# Revit family: 931-10-001 DN50-80
name_source: partatom
category: Pipe Accessories
units: mm (PartAtom-declared; Revit-internal decimal feet)

## family parameters
Always vertical = Yes
Cut with Voids When Loaded = No
Part Type = Valve - Breaks Into
Round Connector Dimension = Use Diameter
Shared = No
Work Plane-Based = No

## types (3) — shared parameters
1 = 1 mm  [stored 0.00328084 ft]
2 = 3 mm  [stored 0.00984252 ft]
Actuator_Flange_R = 45 mm  [stored 0.147638 ft]
Body_Thickness = 6 mm  [stored 0.019685 ft]
Body_dim = 23 mm  [stored 0.0754593 ft]
DN050_PN10/16 = 931-050-10-020040200000
DN065_PN10/16 = 931-065-10-020040200000
DN080_PN10/16 = 931-080-10-020040200000
Description_ = AVK BUTTERFLY VALVE, WAFER, PN10/16
F = 18 mm  [stored 0.0590551 ft]
Flange_T = 19 mm  [stored 0.062336 ft]
G = 11 mm  [stored 0.0360892 ft]
H = 90 mm
Hole = 12 mm  [stored 0.0393701 ft]
Hole_diameter = 10 mm  [stored 0.0328084 ft]
Search_table = 931-10-001 DN50-80
URL_product_pages = https://www.avkvalves.com
base1 = 9 mm  [stored 0.0295276 ft]
hole1 = 6 mm  [stored 0.019685 ft]
wafer = 68 mm
wafer_fillet = 34 mm
zero-valued in all types: Default Elevation

## per-type parameters (varying)
| type | Actuator_FL_T | B | B1 | Body_dim1 | Body_thickness | Bore_R | C | D | DN | E | Flange_R | PCD_R | base | base_dis | disk | disk1 | disk2 | rubber | wafer_F | wafer_X | wafer_X1 | wafer_Y | wafer_dim1 | wafer_dim2 |
| DN050_PN10/16 | 15 mm  [stored 0.0492126 ft] | 27 mm  [stored 0.0885827 ft] | 28 mm  [stored 0.0918635 ft] | 30 mm  [stored 0.0984252 ft] | 29 mm  [stored 0.0951444 ft] | 25 mm  [stored 0.082021 ft] | 43 mm  [stored 0.141076 ft] | 53 mm  [stored 0.173885 ft] | 50 mm  [stored 0.164042 ft] | 140 mm | 83 mm | 63 mm | 15 mm  [stored 0.0492126 ft] | 62 mm  [stored 0.203412 ft] | 2 mm  [stored 0.00656168 ft] | 6 mm  [stored 0.019685 ft] | 53 mm  [stored 0.173885 ft] | 14 mm  [stored 0.0459318 ft] | 23 mm  [stored 0.0754593 ft] | 9 mm  [stored 0.0295276 ft] | 23 mm  [stored 0.0754593 ft] | 5 mm  [stored 0.0164042 ft] | 35 mm  [stored 0.114829 ft] | 44 mm  [stored 0.144357 ft] |
| DN065_PN10/16 | 15 mm  [stored 0.0492126 ft] | 32 mm  [stored 0.104987 ft] | 33 mm  [stored 0.108268 ft] | 32 mm  [stored 0.104987 ft] | 35 mm  [stored 0.114829 ft] | 33 mm  [stored 0.108268 ft] | 46 mm  [stored 0.150919 ft] | 59 mm | 65 mm | 152 mm | 88 mm | 73 mm | 16 mm  [stored 0.0524934 ft] | 69 mm | 3 mm  [stored 0.00984252 ft] | 7 mm  [stored 0.0229659 ft] | 64 mm | 13 mm  [stored 0.0426509 ft] | 28 mm  [stored 0.0918635 ft] | 10 mm  [stored 0.0328084 ft] | 28 mm  [stored 0.0918635 ft] | 5 mm  [stored 0.0164042 ft] | 45 mm  [stored 0.147638 ft] | 42 mm  [stored 0.137795 ft] |
| DN080_PN10/16 | 19 mm  [stored 0.062336 ft] | 39 mm  [stored 0.127953 ft] | 40 mm  [stored 0.131234 ft] | 32 mm  [stored 0.104987 ft] | 42 mm  [stored 0.137795 ft] | 40 mm  [stored 0.131234 ft] | 46 mm  [stored 0.150919 ft] | 65 mm | 80 mm | 159 mm | 97 mm | 77 mm | 16 mm  [stored 0.0524934 ft] | 77 mm | 4 mm  [stored 0.0131234 ft] | 10 mm  [stored 0.0328084 ft] | 78 mm | 13 mm  [stored 0.0426509 ft] | 35 mm  [stored 0.114829 ft] | 10 mm  [stored 0.0328084 ft] | 35 mm  [stored 0.114829 ft] | 9 mm  [stored 0.0295276 ft] | 38 mm  [stored 0.124672 ft] | 45 mm  [stored 0.147638 ft] |

note: [stored X ft] marks values corroborated as IEEE doubles in the binary element streams (Revit-internal decimal feet)

## geometry (parser evidence)
native form markers: Sweep x5
no freeform markers — native parametric forms only
